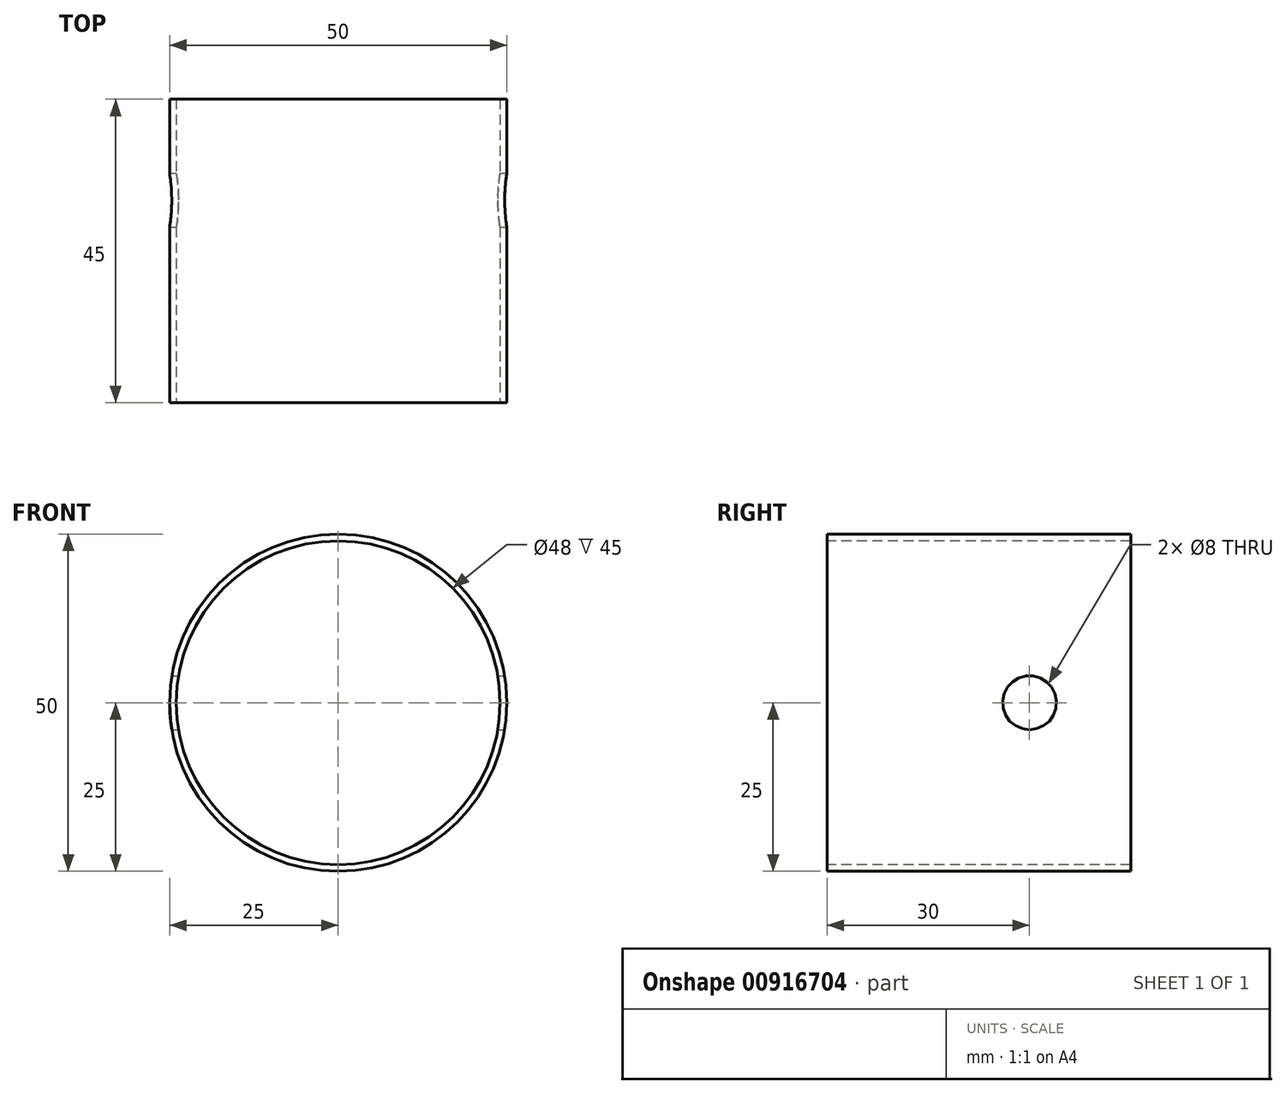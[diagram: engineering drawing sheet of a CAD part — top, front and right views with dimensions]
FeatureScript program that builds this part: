
annotation { "Feature Type Name" : "Feature", "Feature Type Description" : "" }
export const myFeature = defineFeature(function(context is Context, id is Id, definition is map)
    precondition{}
    {
        {
            var Q0;
            Q0=qCreatedBy(makeId("Front.planeOp"),FACE);
            var sketch = newSketch(context, id + "F0", { "sketchPlane" : qUnion([Q0])});
            skCircle(sketch, "E0", {"center": v(0, 0) * mm, "radius": 25 * mm});
            skCircle(sketch, "E1", {"center": v(0, 0) * mm, "radius": 24 * mm});
            skSolve(sketch);
        }
        {
            var Q0;
            Q0=qCreatedBy(makeId("Right.planeOp"),FACE);
            var sketch = newSketch(context, id + "F1", { "sketchPlane" : qUnion([Q0])});
            skLineSegment(sketch, "E2", {"start": v(0, 0) * mm, "end": v(-45, 0) * mm});
            skSolve(sketch);
        }
        {
            var Q0;
            Q0=qSketchRegion(id+"F0",true);
            var Q1;
            Q1=qConstructionFilter(qBodyType(qCreatedBy(id+"F1",EDGE),BodyType.WIRE),ConstructionObject.NO);
            sweep(context, id + "F2", {"profiles" : qUnion([Q0]), "path" : qUnion([Q1])});
        }
        {
            var Q0;
            Q0=qCreatedBy(makeId("Right.planeOp"),FACE);
            var sketch = newSketch(context, id + "F3", { "sketchPlane" : qUnion([Q0])});
            skCircle(sketch, "E3", {"center": v(-15, 0) * mm, "radius": 4 * mm});
            skSolve(sketch);
        }
        {
            var Q0;
            Q0=qCreatedBy(makeId("Top.planeOp"),FACE);
            var sketch = newSketch(context, id + "F4", { "sketchPlane" : qUnion([Q0])});
            skLineSegment(sketch, "E4", {"start": v(40, -15) * mm, "end": v(-40, -15) * mm});
            skSolve(sketch);
        }
        {
            var Q0;
            Q0=qSketchRegion(id+"F3",true);
            var Q1;
            Q1=sQuery(id+"F3.wireOp",EDGE,"E3");
            var Q2;
            Q2=qConstructionFilter(qBodyType(qCreatedBy(id+"F4",EDGE),BodyType.WIRE),ConstructionObject.NO);
            sweep(context, id + "F5", {"operationType" : NewBodyOperationType.REMOVE, "profiles" : qUnion([Q0]), "surfaceProfiles" : qUnion([Q1]), "path" : qUnion([Q2])});
        }
    });
